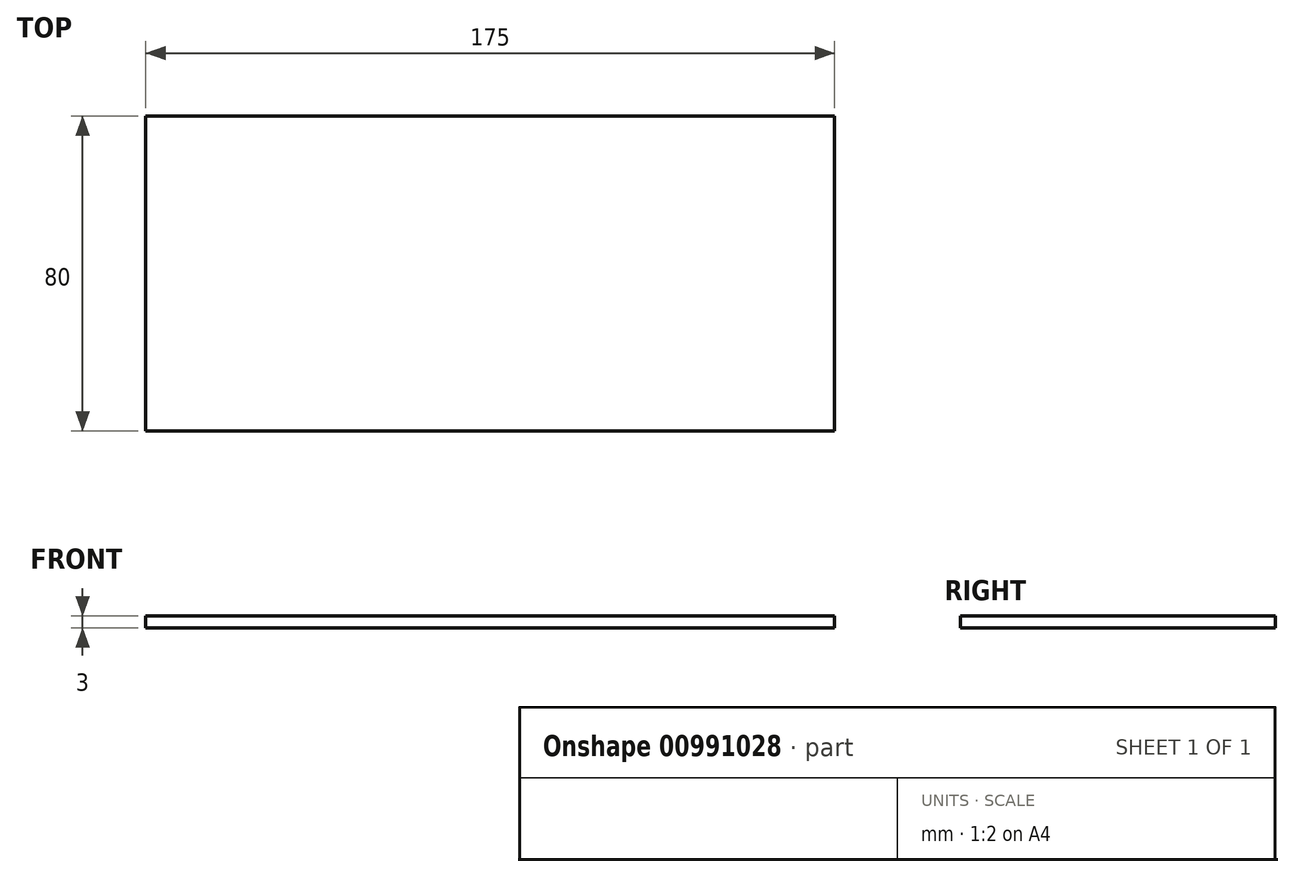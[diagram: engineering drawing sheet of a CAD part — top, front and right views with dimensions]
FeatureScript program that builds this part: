
annotation { "Feature Type Name" : "Feature", "Feature Type Description" : "" }
export const myFeature = defineFeature(function(context is Context, id is Id, definition is map)
    precondition{}
    {
        {
            var Q0;
            Q0=qCreatedBy(makeId("Top.planeOp"),FACE);
            var sketch = newSketch(context, id + "F0", { "sketchPlane" : qUnion([Q0])});
            skLineSegment(sketch, "E0.bottom", {"start": v(87.5, -40) * mm, "end": v(-87.5, -40) * mm});
            skLineSegment(sketch, "E0.top", {"start": v(87.5, 40) * mm, "end": v(-87.5, 40) * mm});
            skLineSegment(sketch, "E0.left", {"start": v(87.5, -40) * mm, "end": v(87.5, 40) * mm});
            skLineSegment(sketch, "E0.right", {"start": v(-87.5, -40) * mm, "end": v(-87.5, 40) * mm});
            skPoint(sketch, "E0.middle", {"position": v(0, 0) * mm});
            skSolve(sketch);
        }
        {
            var Q0;
            Q0 = qSketchRegion(id + "F0", true);
            extrude(context, id + "F1", {"entities" : qUnion([Q0]), "depth" : 3 * mm, "offsetDistance" : 25 * mm});
        }
    });
